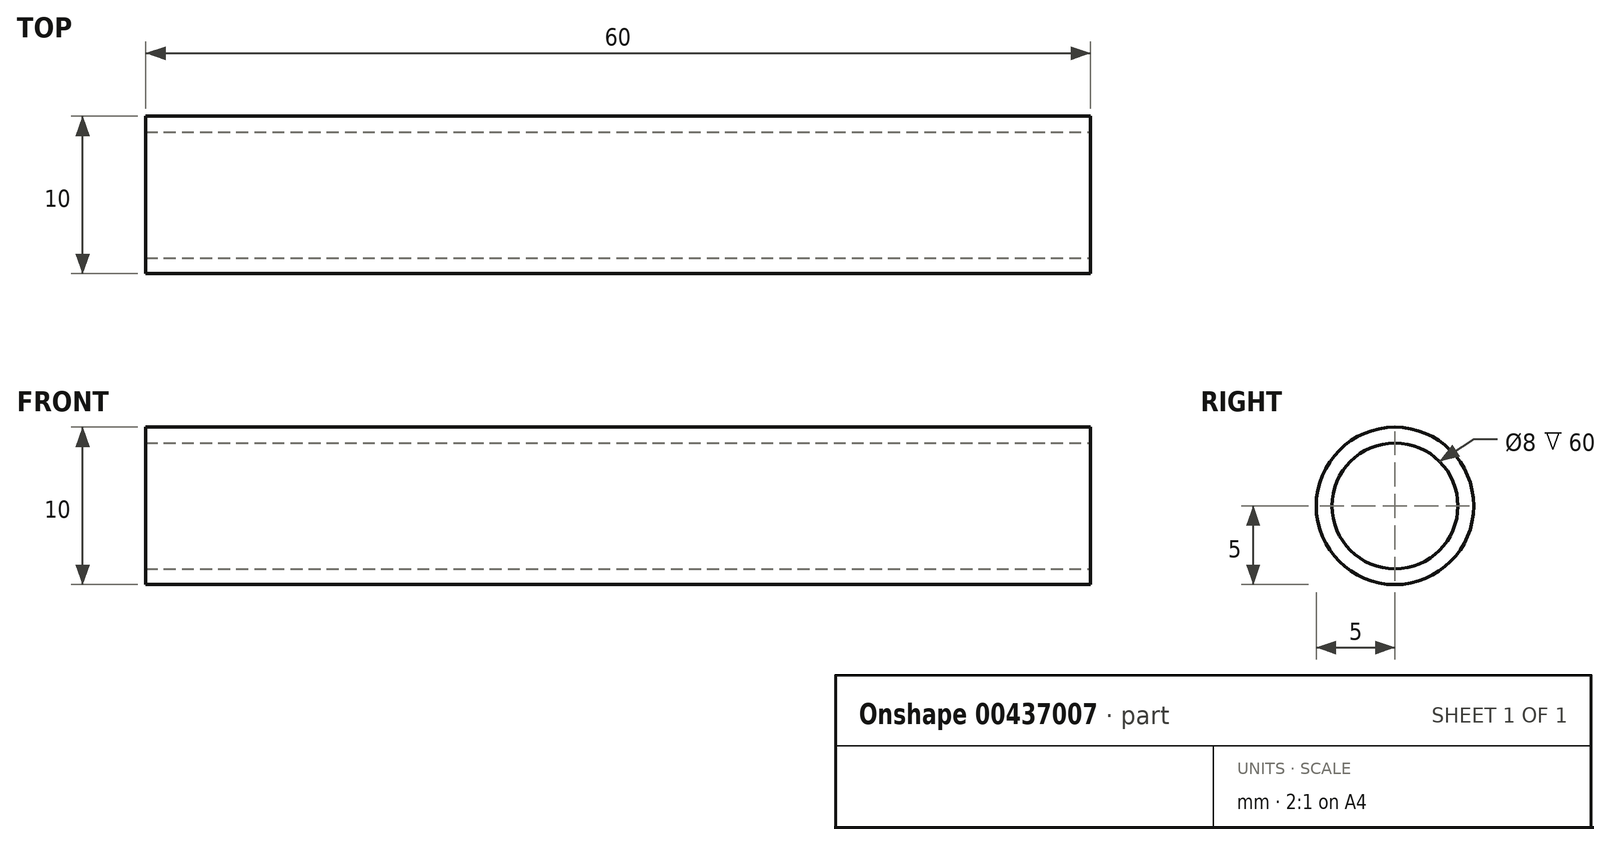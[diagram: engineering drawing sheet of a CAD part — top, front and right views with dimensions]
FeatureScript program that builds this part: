
annotation { "Feature Type Name" : "Feature", "Feature Type Description" : "" }
export const myFeature = defineFeature(function(context is Context, id is Id, definition is map)
    precondition{}
    {
        {
            var Q0;
            Q0=qCreatedBy(makeId("Top.planeOp"),FACE);
            var sketch = newSketch(context, id + "F0", { "sketchPlane" : qUnion([Q0])});
            skLineSegment(sketch, "E0", {"start": v(0, 5) * mm, "end": v(-60, 5) * mm});
            skLineSegment(sketch, "E1", {"start": v(-60, 5) * mm, "end": v(-60, 4) * mm});
            skLineSegment(sketch, "E2", {"start": v(-60, 4) * mm, "end": v(0, 4) * mm});
            skLineSegment(sketch, "E3", {"start": v(0, 0) * mm, "end": v(-50.95, 0) * mm, "construction": true});
            skLineSegment(sketch, "E4", {"start": v(0, 4) * mm, "end": v(0, 5) * mm});
            skSolve(sketch);
        }
        {
            var Q0;
            Q0 = qSketchRegion(id + "F0", true);
            var Q1;
            Q1=sQuery(id+"F0.wireOp",EDGE,"E3");
            revolve(context, id + "F1", {"entities" : qUnion([Q0]), "axis" : qUnion([Q1]), "revolveType" : RevolveType.FULL});
        }
    });
